FCSTD DOCUMENT  (FreeCAD 0.19R24366 (Git))
Label: Single lever solution common pivot
License: All rights reserved
LicenseURL: http://en.wikipedia.org/wiki/All_rights_reserved
objects: Sketcher::SketchObject×1, PartDesign::Body×1
note: 2 computed .brp shape members not serialized (recipe doc carries the construction recipe); baked Part::Feature solids carry a one-line shape summary decoded from their .brp

FEATURE [Sketcher::SketchObject] Sketch
  FullyConstrained = true
  MapMode = 5
  Support = -> [XY_Plane]
  sketch-geometry (20):
    g0: LineSegment StartX=710.218 StartY=0 StartZ=0 EndX=730.218 EndY=49.6455 EndZ=0
    g1: LineSegment StartX=750.218 StartY=0 StartZ=0 EndX=730.218 EndY=49.6458 EndZ=0
    g2: LineSegment StartX=430.41 StartY=316.58 StartZ=0 EndX=730.218 EndY=49.6458 EndZ=0
    g3: LineSegment StartX=699.176 StartY=449.864 StartZ=0 EndX=730.218 EndY=49.6455 EndZ=0
    g4: LineSegment StartX=730.218 StartY=49.6455 StartZ=0 EndX=737.692 EndY=68.1967 EndZ=0
    g5: LineSegment StartX=730.218 StartY=49.6458 StartZ=0 EndX=722.745 EndY=68.197 EndZ=0
    g6: LineSegment StartX=737.692 StartY=68.1967 StartZ=0 EndX=728.492 EndY=71.903 EndZ=0
    g7: LineSegment StartX=722.745 StartY=68.197 StartZ=0 EndX=713.545 EndY=64.4908 EndZ=0
    g8: ArcOfCircle CenterX=750.218 CenterY=0 CenterZ=0 NormalX=0 NormalY=0 NormalZ=1 AngleXU=0 Radius=40 StartAngle=3.14159 EndAngle=6.28319
    g9: ArcOfCircle CenterX=750.218 CenterY=0 CenterZ=0 NormalX=0 NormalY=0 NormalZ=1 AngleXU=0 Radius=160 StartAngle=3.14159 EndAngle=6.28319
    g10: LineSegment StartX=710.218 StartY=0 StartZ=0 EndX=699.176 EndY=449.864 EndZ=0
    g11: LineSegment StartX=750.218 StartY=0 StartZ=0 EndX=430.41 EndY=316.58 EndZ=0
    g12: LineSegment StartX=730.218 StartY=49.6455 StartZ=0 EndX=709.012 EndY=49.125 EndZ=0
    g13: LineSegment StartX=730.218 StartY=49.6458 StartZ=0 EndX=715.295 EndY=34.5703 EndZ=0
    g14: LineSegment StartX=0 StartY=0 StartZ=0 EndX=730.218 EndY=49.6455 EndZ=0
    g15: LineSegment StartX=730.218 StartY=49.6458 StartZ=0 EndX=0 EndY=0 EndZ=0
    g16: LineSegment StartX=0 StartY=0 StartZ=0 EndX=-6.7831 EndY=99.7697 EndZ=0
    g17: LineSegment StartX=0 StartY=0 StartZ=0 EndX=-6.78307 EndY=99.7697 EndZ=0
    g18: LineSegment StartX=-6.78307 StartY=99.7697 StartZ=0 EndX=699.176 EndY=449.864 EndZ=0
    g19: LineSegment StartX=430.41 StartY=316.58 StartZ=0 EndX=-6.7831 EndY=99.7697 EndZ=0
  constraints (66):
    c: PointOnObject(g0,g-1)
    c: PointOnObject(g1,g-1)
    c: Equal(g0,g1)
    c: Coincident(g2,g1)
    c: Coincident(g3,g0)
    c: Coincident(g4,g0)
    c: Coincident(g5,g1)
    c: Distance(g4) = 20
    c: Distance(g5) = 20
    c: Parallel(g0,g4)
    c: Parallel(g1,g5)
    c: Coincident(g6,g4)
    c: PointOnObject(g6,g3)
    c: Coincident(g7,g5)
    c: PointOnObject(g7,g2)
    c: Perpendicular(g7,g5)
    c: Perpendicular(g6,g4)
    c: Equal(g6,g7)
    c: Equal(g2,g3)
    c: Distance(g0,g3) = 450
    c: Coincident(g8,g1)
    c: Radius(g8) = 40
    c: PointOnObject(g9,g-1)
    c: PointOnObject(g8,g-1)
    c: PointOnObject(g8,g-1)
    c: PointOnObject(g9,g-1)
    c: Radius(g9) = 160
    c: Coincident(g9,g1)
    c: Coincident(g10,g0)
    c: Coincident(g11,g1)
    c: DistanceX(g-1,g1) = 750.218
    c: Distance(g0) = 53.5228
    c: Distance(g3) = 401.421
    c: Angle(g0,g-1) = 1.95377
    c: Angle(g1,g-1) = 1.18784
    c: Coincident(g12,g0)
    c: PointOnObject(g12,g10)
    c: Perpendicular(g10,g12)
    c: Coincident(g13,g1)
    c: PointOnObject(g13,g11)
    c: Perpendicular(g11,g13)
    c: Distance(g12) = 21.2125
    c: Coincident(g14,g-1)
    c: Coincident(g14,g0)
    c: Coincident(g15,g1)
    c: Coincident(g15,g14)
    c: Coincident(g16,g14)
    c: Coincident(g17,g14)
    c: Perpendicular(g14,g17)
    c: Perpendicular(g15,g16)
    c: Distance(g16) = 100
    c: Equal(g17,g16)
    c: Coincident(g18,g17)
    c: Coincident(g18,g3)
    c: Coincident(g19,g2)
    c: Coincident(g19,g16)
    c: Distance(g19) = 488
    c: Distance(g18) = 788
    c: Equal(g14,g15)
    c: Distance(g15) = 731.904
    c: Coincident(g11,g2)
    c: Coincident(g10,g3)
    c: Angle(g19,g2) = 1.95376
    c: Angle(g18,g3) = 1.18783
    c: DistanceX(g0,g1) = 40
    c: DistanceY(g-1,g0) = 49.6455
FEATURE [PartDesign::Body] Body
  Group = -> [Sketch]
  Origin = -> Origin
